# Revit family: Ceiling_Sensor-Low_Voltage_PIR-Hubbell_Wiring-LVPR1500R
name_source: partatom
category: Lighting Devices
revit_build: Autodesk Revit 2015 (Build: 20140606_1530(x64)
units: mm (PartAtom-declared; Revit-internal decimal feet)

## types (3) — shared parameters
Ambient Light = 1 to 1000 foot candles
Connector Description 1 = Power Supply
Connector Description 2 = Controls
Coverage = 360.00°
Default Elevation = 48 "
Description = Low Profile, Line Voltage Passive Infrared - Adaptive Technology
Device Material = Plastic - Hubbell - White
Glass = Plastic - Hubbell - Polyethylene
Load Classification = Lighting
Manufacturer = Hubbell Wiring Device-Kellems
Model = LVPR1500R
Number of Poles = 1
Operating Temperature = 32°F to 104°F (0°C to 40°C) with rate of change not
exceeding 20°F (11°C) per hour
Power Factor = 1
Product Documentation Link = http://ecatalog.hubbell-wiring.com
Product Page URL = http://ecatalog.hubbell-wiring.com
Product data url = https://bimobject.com
Sensitivity = Manual, 0 to 100%
Storage Temperature = -20°F to 150°F (-29°C to 65°C); 0% to 95%
non-condensing relative humidity
Time Delay = Manual 30 seconds to 30 minutes
URL = http://www.hubbell-wiring.com

## per-type parameters (varying)
| type | Apparent Load | Voltage |
| 120V | 1000.000 VA | 120 V |
| 277V | 1800.000 VA | 277 V |
| 347V | 2200.000 VA | 347 V |

## geometry (parser evidence)
native form markers: Blend x4, Sweep x5
no freeform markers — native parametric forms only
